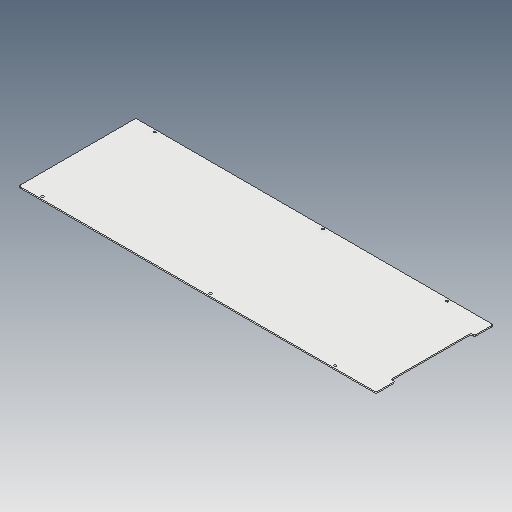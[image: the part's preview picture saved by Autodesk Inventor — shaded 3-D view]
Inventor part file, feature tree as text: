
AUTODESK INVENTOR PART (.ipt)
format: ipt  version: 2023.5 (Build 275446000, 446)  size: 95,744 bytes
history: native  units: in
note: dims shown in document units (in); Inventor stores cm internally (conversion verified against a paired STEP export)
features: fillet x1
ambient origin geometry x8: Origin, YZ Plane, XZ Plane, XY Plane, X Axis, Y Axis, Z Axis, Center Point
bodies: Solid1 (feature_tree)
feature tree (1):
  fillet  "Fillet2"  [1 undecoded]
note: 1 required parameter value undecoded (feature->parameter linkage not recoverable at this tier; creation-order binding heuristic only, values carry confidence <= 0.55)
